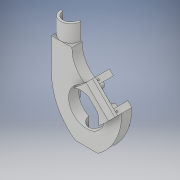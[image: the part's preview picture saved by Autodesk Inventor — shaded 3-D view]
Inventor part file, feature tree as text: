
AUTODESK INVENTOR PART (.ipt)
format: ipt  version: 2019 (Build 230136000, 136)  size: 591,360 bytes
history: native  units: mm
features: sketch x21, extrude x17, projected_geometry x3, sweep x2, other x2, fillet x2
ambient origin geometry x8: Origin, YZ Plane, XZ Plane, XY Plane, X Axis, Y Axis, Z Axis, Center Point
bodies: Body1 (feature_tree)
feature tree (47):
  extrude  "Extrusion2"  Depth=80.0mm
  sketch  "Esquisse3"
  sweep  "Balayage1"
  extrude  "Extrusion6"  Depth=32.0mm
  extrude  "Extrusion7"  Depth=18.0mm TaperAngle=0.0deg
  extrude  "Extrusion8"  TaperAngle=135.0deg  [1 undecoded]
  sketch  "Esquisse11"
  sketch  "Esquisse12"
  other  "Plan de construction1"
  sketch  "Esquisse13"
  extrude  "Extrusion9"  Depth=23.0mm
  extrude  "Extrusion10"  Depth=14.0mm
  other  "Plan de construction2"
  sketch  "Esquisse14"
  extrude  "Extrusion11"  Depth=4.0mm
  extrude  "Extrusion12"  TaperAngle=0.0deg  [1 undecoded]
  extrude  "Extrusion13"  Depth=4.0mm TaperAngle=0.0deg
  extrude  "Extrusion14"  Depth=9.0mm
  extrude  "Extrusion15"  Depth=4.0mm TaperAngle=0.0deg
  sketch  "Esquisse20"
  sketch  "Esquisse21"
  sketch  "Esquisse24"
  extrude  "Extrusion17"  Depth=2.0mm
  sweep  "Balayage4"
  extrude  "Extrusion18"  Depth=35.0mm
  extrude  "Extrusion19"  Depth=17.5mm
  extrude  "Extrusion20"  Depth=8.5mm
  extrude  "Extrusion21"  Depth=12.0mm TaperAngle=0.0deg
  fillet  "Congé1"  Radius=30.0mm
  extrude  "Extrusion22"  Depth=28.0mm
  fillet  "Congé2"  Radius=17.0mm
  sketch  "Esquisse2"
  sketch  "Esquisse4"
  sketch  "Esquisse8"
  sketch  "Esquisse9"
  sketch  "Esquisse10"
  sketch  "Esquisse16"
  projected_geometry  "Boucle projetée3"
  sketch  "Esquisse18"
  sketch  "Esquisse19"
  projected_geometry  "Boucle projetée4"
  projected_geometry  "Boucle projetée6"
  sketch  "Esquisse25"
  sketch  "Esquisse26"
  sketch  "Esquisse27"
  sketch  "Esquisse28"
  sketch  "Esquisse29"
note: 2 required parameter values undecoded (feature->parameter linkage not recoverable at this tier; creation-order binding heuristic only, values carry confidence <= 0.55)
